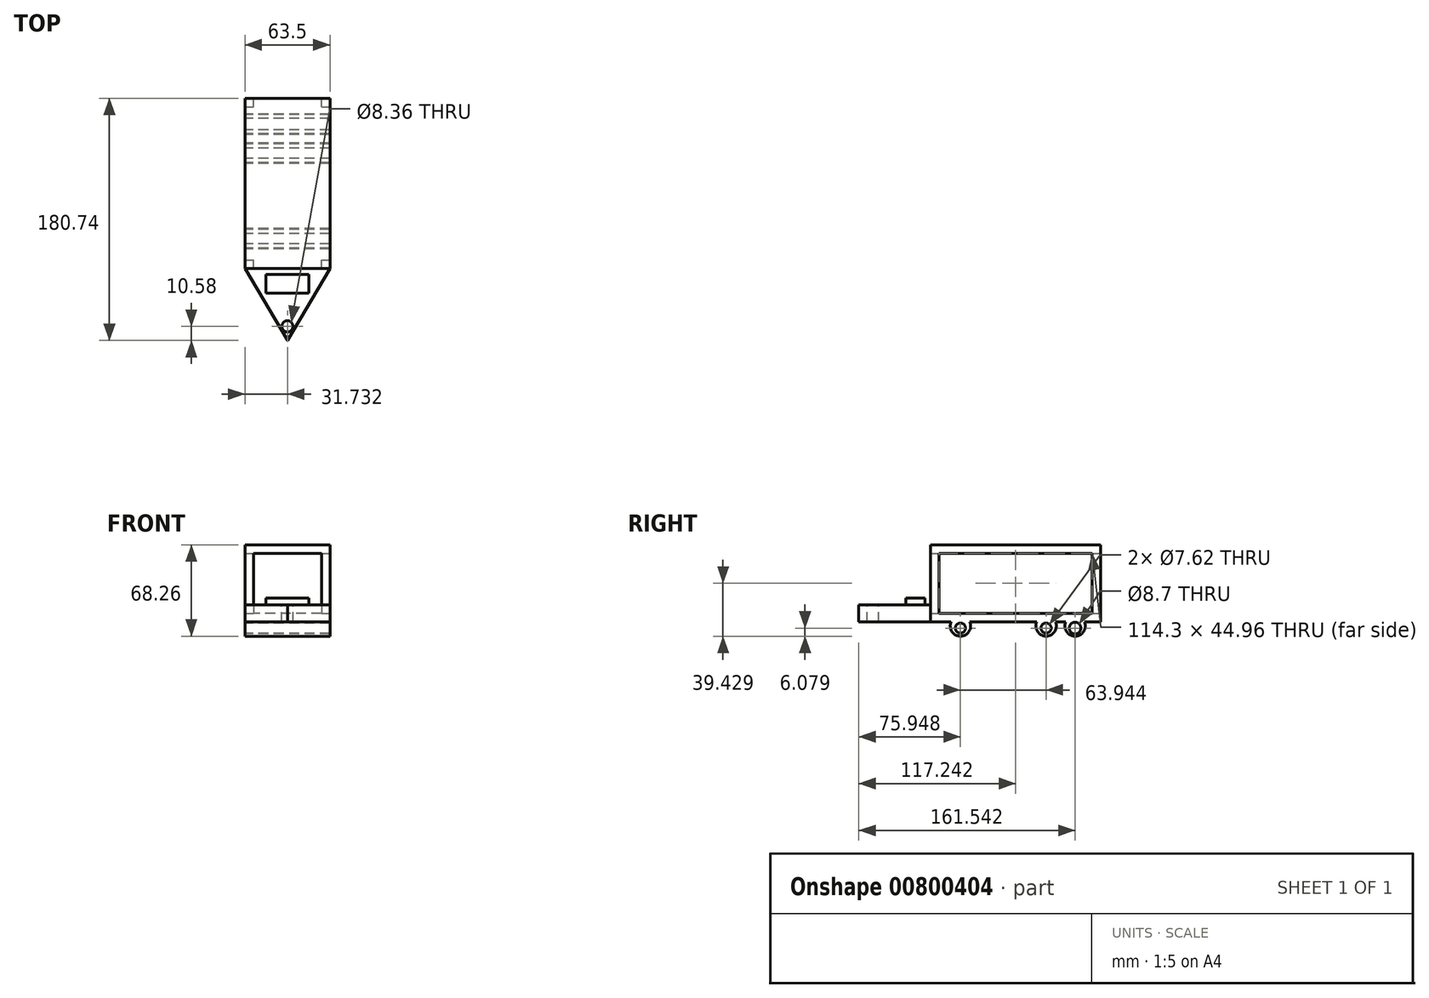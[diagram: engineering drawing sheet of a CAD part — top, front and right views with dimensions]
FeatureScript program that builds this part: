
annotation { "Feature Type Name" : "Feature", "Feature Type Description" : "" }
export const myFeature = defineFeature(function(context is Context, id is Id, definition is map)
    precondition{}
    {
        {
            var Q0;
            Q0=qCreatedBy(makeId("Top.planeOp"),FACE);
            var sketch = newSketch(context, id + "F0", { "sketchPlane" : qUnion([Q0])});
            skLineSegment(sketch, "E0", {"start": v(-27.56, 101.28) * mm, "end": v(-27.56, -25.72) * mm});
            skLineSegment(sketch, "E1", {"start": v(-27.56, -25.72) * mm, "end": v(35.94, -25.72) * mm});
            skLineSegment(sketch, "E2", {"start": v(35.94, -25.72) * mm, "end": v(35.94, 101.28) * mm});
            skLineSegment(sketch, "E3", {"start": v(35.94, 101.28) * mm, "end": v(-27.56, 101.28) * mm});
            skSolve(sketch);
        }
        {
            var Q0;
            Q0=makeQuery(id+"F0.imprint","IMPRINT",FACE,{"disambiguationData":[TD([[makeQuery(id+"F0.imprint","IMPRINT",EDGE,{"derivedFrom":sQuery(id+"F0.wireOp",EDGE,"E0")}),1.0]])]});
            extrude(context, id + "F1", {"entities" : qUnion([Q0]), "depth" : 57.66 * mm, "offsetDistance" : 25.4 * mm});
        }
        {
            var Q0;
            Q0=makeQuery(id+"F1.opExtrude","CAP_FACE",FACE,{"disambiguationData":[OSD([sQuery(id+"F0.wireOp",EDGE,"E0"),sQuery(id+"F0.wireOp",EDGE,"E1"),sQuery(id+"F0.wireOp",EDGE,"E2"),sQuery(id+"F0.wireOp",EDGE,"E3")])],"isStart":false});
            var sketch = newSketch(context, id + "F2", { "sketchPlane" : qUnion([Q0])});
            skLineSegment(sketch, "E4.0", {"start": v(-21.21, -19.37) * mm, "end": v(29.59, -19.37) * mm});
            skLineSegment(sketch, "E5.0", {"start": v(-21.21, 94.93) * mm, "end": v(-21.21, -19.37) * mm});
            skLineSegment(sketch, "E6.0", {"start": v(29.59, 94.93) * mm, "end": v(-21.21, 94.93) * mm});
            skLineSegment(sketch, "E7.0", {"start": v(29.59, -19.37) * mm, "end": v(29.59, 94.93) * mm});
            skSolve(sketch);
        }
        {
            var Q0;
            Q0=makeQuery(id+"F2.imprint","IMPRINT",FACE,{"disambiguationData":[TD([[makeQuery(id+"F2.imprint","IMPRINT",EDGE,{"derivedFrom":sQuery(id+"F2.wireOp",EDGE,"E4.0")}),1.0]])]});
            extrude(context, id + "F3", {"entities" : qUnion([Q0]), "operationType" : NewBodyOperationType.REMOVE, "oppositeDirection" : true, "depth" : 155.7 * mm, "offsetDistance" : 25.4 * mm});
        }
        {
            var Q0;
            Q0=makeQuery(id+"F1.opExtrude","SWEPT_FACE",FACE,{"disambiguationData":[OSD([sQuery(id+"F0.wireOp",EDGE,"E2")])]});
            var sketch = newSketch(context, id + "F4", { "sketchPlane" : qUnion([Q0])});
            skLineSegment(sketch, "E8.0", {"start": v(-19.37, 101.6) * mm, "end": v(-19.37, 0) * mm});
            skLineSegment(sketch, "E9.0", {"start": v(-25.72, 6.35) * mm, "end": v(101.28, 6.35) * mm});
            skLineSegment(sketch, "E10.0", {"start": v(94.93, 101.6) * mm, "end": v(94.93, 0) * mm});
            skLineSegment(sketch, "E11.0", {"start": v(-25.72, 51.3) * mm, "end": v(101.28, 51.3) * mm});
            skSolve(sketch);
        }
        {
            var Q0;
            {var subQ0=sQuery(id+"F4.wireOp",EDGE,"E11.0");var subQ1=sQuery(id+"F4.wireOp",EDGE,"E8.0");var subQ2=makeQuery(id+"F4.imprint","INTERSECT",VERTEX,{"derivedFrom":[subQ1,subQ0]});Q0=makeQuery(id+"F4.imprint","IMPRINT",FACE,{"disambiguationData":[TD([[makeQuery(id+"F4.imprint","IMPRINT",EDGE,{"disambiguationData":[TD([[subQ2,-1.0]])],"derivedFrom":subQ1}),1.0]])]});}
            extrude(context, id + "F5", {"entities" : qUnion([Q0]), "operationType" : NewBodyOperationType.REMOVE, "oppositeDirection" : true, "depth" : 96.77 * mm, "offsetDistance" : 25.4 * mm});
        }
        {
            var Q0;
            Q0=makeQuery(id+"F1.opExtrude","SWEPT_FACE",FACE,{"disambiguationData":[OSD([sQuery(id+"F0.wireOp",EDGE,"E3")])]});
            var sketch = newSketch(context, id + "F6", { "sketchPlane" : qUnion([Q0])});
            skLineSegment(sketch, "E12.0", {"start": v(-35.94, 51.3) * mm, "end": v(27.56, 51.3) * mm});
            skLineSegment(sketch, "E13.0", {"start": v(-29.59, 101.6) * mm, "end": v(-29.59, 0) * mm});
            skLineSegment(sketch, "E14.0", {"start": v(-35.94, 6.35) * mm, "end": v(27.56, 6.35) * mm});
            skLineSegment(sketch, "E15.0", {"start": v(21.21, 101.6) * mm, "end": v(21.21, 0) * mm});
            skSolve(sketch);
        }
        {
            var Q0;
            {var subQ0=sQuery(id+"F6.wireOp",EDGE,"E13.0");var subQ1=sQuery(id+"F6.wireOp",EDGE,"E12.0");var subQ2=makeQuery(id+"F6.imprint","INTERSECT",VERTEX,{"derivedFrom":[subQ1,subQ0]});Q0=makeQuery(id+"F6.imprint","IMPRINT",FACE,{"disambiguationData":[TD([[makeQuery(id+"F6.imprint","IMPRINT",EDGE,{"disambiguationData":[TD([[subQ2,-1.0]])],"derivedFrom":subQ1}),-1.0]])]});}
            extrude(context, id + "F7", {"entities" : qUnion([Q0]), "operationType" : NewBodyOperationType.REMOVE, "oppositeDirection" : true, "depth" : 127 * mm, "offsetDistance" : 25.4 * mm});
        }
        {
            var Q0;
            {var subQ2=makeQuery(id+"F3.boolean.opBoolean","COPY",FACE,{"derivedFrom":makeQuery(id+"F3.opExtrude","SWEPT_FACE",FACE,{"disambiguationData":[OSD([sQuery(id+"F2.wireOp",EDGE,"E4.0")])]})});var subQ4=makeQuery(id+"F5.opExtrude","SWEPT_FACE",FACE,{"disambiguationData":[OSD([sQuery(id+"F4.wireOp",EDGE,"E8.0")])]});var subQ5=sQuery(id+"F0.wireOp",EDGE,"E0");var subQ8=sQuery(id+"F0.wireOp",EDGE,"E2");Q0=makeQuery(id+"F7.boolean.opBoolean","SPLIT",FACE,{"disambiguationData":[TD([makeQuery(id+"F1.opExtrude","CAP_FACE",FACE,{"disambiguationData":[OSD([subQ5,sQuery(id+"F0.wireOp",EDGE,"E1"),subQ8,sQuery(id+"F0.wireOp",EDGE,"E3")])],"isStart":true})])],"derivedFrom":makeQuery(id+"F5.boolean.opBoolean","MERGE",FACE,{"derivedFrom":[subQ2,subQ4]})});}
            extrude(context, id + "F8", {"entities" : qUnion([Q0]), "operationType" : NewBodyOperationType.ADD, "depth" : 120.14 * mm, "offsetDistance" : 25.4 * mm});
        }
        {
            var Q0;
            {var subQ1=makeQuery(id+"F5.opExtrude","SWEPT_FACE",FACE,{"disambiguationData":[OSD([sQuery(id+"F4.wireOp",EDGE,"E8.0")])]});var subQ2=makeQuery(id+"F3.boolean.opBoolean","COPY",FACE,{"derivedFrom":makeQuery(id+"F3.opExtrude","SWEPT_FACE",FACE,{"disambiguationData":[OSD([sQuery(id+"F2.wireOp",EDGE,"E4.0")])]})});var subQ4=sQuery(id+"F0.wireOp",EDGE,"E2");var subQ5=sQuery(id+"F0.wireOp",EDGE,"E0");Q0=makeQuery(id+"F7.boolean.opBoolean","SPLIT",FACE,{"disambiguationData":[TD([makeQuery(id+"F1.opExtrude","CAP_FACE",FACE,{"disambiguationData":[OSD([subQ5,sQuery(id+"F0.wireOp",EDGE,"E1"),subQ4,sQuery(id+"F0.wireOp",EDGE,"E3")])],"isStart":false})])],"derivedFrom":makeQuery(id+"F5.boolean.opBoolean","MERGE",FACE,{"derivedFrom":[subQ2,subQ1]})});}
            extrude(context, id + "F9", {"entities" : qUnion([Q0]), "operationType" : NewBodyOperationType.ADD, "depth" : 115.82 * mm, "offsetDistance" : 25.4 * mm});
        }
        {
            var Q0;
            Q0=qCreatedBy(makeId("Top.planeOp"),FACE);
            var sketch = newSketch(context, id + "F10", { "sketchPlane" : qUnion([Q0])});
            skLineSegment(sketch, "E16.0", {"start": v(-27.56, -25.72) * mm, "end": v(35.94, -25.72) * mm});
            skLineSegment(sketch, "E17", {"start": v(4.19, -25.72) * mm, "end": v(4.19, -79.46) * mm});
            skLineSegment(sketch, "E18", {"start": v(4.19, -79.46) * mm, "end": v(-27.56, -25.72) * mm});
            skLineSegment(sketch, "E19", {"start": v(35.94, -25.72) * mm, "end": v(4.19, -79.46) * mm});
            skSolve(sketch);
        }
        {
            var Q0;
            Q0=qSketchRegion(id+"F10",true);
            extrude(context, id + "F11", {"entities" : qUnion([Q0]), "operationType" : NewBodyOperationType.ADD, "depth" : 12.7 * mm, "offsetDistance" : 25.4 * mm});
        }
        {
            var Q0;
            Q0=makeQuery(id+"F11.opExtrude","CAP_FACE",FACE,{"disambiguationData":[OSD([sQuery(id+"F10.wireOp",EDGE,"E16.0"),sQuery(id+"F10.wireOp",EDGE,"E18"),sQuery(id+"F10.wireOp",EDGE,"E19")])],"isStart":false});
            var sketch = newSketch(context, id + "F12", { "sketchPlane" : qUnion([Q0])});
            skCircle(sketch, "E20", {"center": v(4.17, -68.88) * mm, "radius": 4.18 * mm});
            skLineSegment(sketch, "E21.0", {"start": v(-21.21, -25.72) * mm, "end": v(29.59, -25.72) * mm});
            skLineSegment(sketch, "E22.0", {"start": v(35.94, -25.72) * mm, "end": v(4.19, -79.46) * mm});
            skLineSegment(sketch, "E23.0", {"start": v(4.19, -79.46) * mm, "end": v(-27.56, -25.72) * mm});
            skLineSegment(sketch, "E24", {"start": v(4.19, -25.72) * mm, "end": v(4.19, -79.46) * mm});
            skSolve(sketch);
        }
        {
            var Q0;
            {var subQ0=sQuery(id+"F12.wireOp",EDGE,"E24");var subQ1=sQuery(id+"F12.wireOp",EDGE,"E20");var subQ2=makeQuery(id+"F12.imprint","INTERSECT",VERTEX,{"disambiguationData":[OD(0.0)],"derivedFrom":[subQ1,subQ0]});Q0=makeQuery(id+"F12.imprint","IMPRINT",FACE,{"disambiguationData":[TD([[makeQuery(id+"F12.imprint","IMPRINT",EDGE,{"disambiguationData":[TD([[subQ2,-1.0]])],"derivedFrom":subQ1}),1.0]])]});}
            var Q1;
            {var subQ0=sQuery(id+"F12.wireOp",EDGE,"E24");var subQ1=sQuery(id+"F12.wireOp",EDGE,"E20");var subQ2=makeQuery(id+"F12.imprint","INTERSECT",VERTEX,{"disambiguationData":[OD(0.0)],"derivedFrom":[subQ1,subQ0]});Q1=makeQuery(id+"F12.imprint","IMPRINT",FACE,{"disambiguationData":[TD([[makeQuery(id+"F12.imprint","IMPRINT",EDGE,{"disambiguationData":[TD([[subQ2,1.0]])],"derivedFrom":subQ1}),1.0]])]});}
            extrude(context, id + "F13", {"entities" : qUnion([Q0, Q1]), "operationType" : NewBodyOperationType.REMOVE, "oppositeDirection" : true, "depth" : 25.4 * mm, "offsetDistance" : 25.4 * mm});
        }
        {
            var Q0;
            Q0=makeQuery(id+"F11.opExtrude","CAP_FACE",FACE,{"disambiguationData":[OSD([sQuery(id+"F10.wireOp",EDGE,"E16.0"),sQuery(id+"F10.wireOp",EDGE,"E18"),sQuery(id+"F10.wireOp",EDGE,"E19")])],"isStart":false});
            var sketch = newSketch(context, id + "F14", { "sketchPlane" : qUnion([Q0])});
            skLineSegment(sketch, "E25.bottom", {"start": v(-11.82, -29.99) * mm, "end": v(20.03, -29.99) * mm});
            skLineSegment(sketch, "E25.top", {"start": v(-11.82, -44.18) * mm, "end": v(20.03, -44.18) * mm});
            skLineSegment(sketch, "E25.left", {"start": v(-11.82, -29.99) * mm, "end": v(-11.82, -44.18) * mm});
            skLineSegment(sketch, "E25.right", {"start": v(20.03, -29.99) * mm, "end": v(20.03, -44.18) * mm});
            skSolve(sketch);
        }
        {
            var Q0;
            Q0=qSketchRegion(id+"F14",true);
            extrude(context, id + "F15", {"entities" : qUnion([Q0]), "operationType" : NewBodyOperationType.ADD, "depth" : 5.08 * mm, "offsetDistance" : 25.4 * mm});
        }
        {
            var Q0;
            Q0=makeQuery(id+"F1.opExtrude","SWEPT_FACE",FACE,{"disambiguationData":[OSD([sQuery(id+"F0.wireOp",EDGE,"E0")])]});
            var sketch = newSketch(context, id + "F16", { "sketchPlane" : qUnion([Q0])});
            skArc(sketch, "E26", {"start": v(-89.1, 0) * mm, "mid": v(-82.08, -10.6) * mm, "end": v(-75.07, 0) * mm});
            skArc(sketch, "E27", {"start": v(-67.45, 0) * mm, "mid": v(-60.43, -10.6) * mm, "end": v(-53.42, 0) * mm});
            skArc(sketch, "E28", {"start": v(-3.5, 0) * mm, "mid": v(3.51, -10.6) * mm, "end": v(10.53, 0) * mm});
            skCircle(sketch, "E29", {"center": v(-82.08, -4.52) * mm, "radius": 4.35 * mm});
            skCircle(sketch, "E30", {"center": v(-60.43, -4.52) * mm, "radius": 3.81 * mm});
            skCircle(sketch, "E31", {"center": v(3.51, -4.52) * mm, "radius": 3.81 * mm});
            skSolve(sketch);
        }
        {
            var Q0;
            Q0=qSketchRegion(id+"F16",true);
            var Q1;
            {var subQ0=sQuery(id+"F16.wireOp",EDGE,"E26");Q1=makeQuery(id+"F16.imprint","IMPRINT",FACE,{"disambiguationData":[TD([[makeQuery(id+"F16.imprint","IMPRINT",EDGE,{"derivedFrom":subQ0}),1.0]])]});}
            var Q2;
            {var subQ0=sQuery(id+"F16.wireOp",EDGE,"E27");Q2=makeQuery(id+"F16.imprint","IMPRINT",FACE,{"disambiguationData":[TD([[makeQuery(id+"F16.imprint","IMPRINT",EDGE,{"derivedFrom":subQ0}),1.0]])]});}
            var Q3;
            {var subQ0=sQuery(id+"F16.wireOp",EDGE,"E28");Q3=makeQuery(id+"F16.imprint","IMPRINT",FACE,{"disambiguationData":[TD([[makeQuery(id+"F16.imprint","IMPRINT",EDGE,{"derivedFrom":subQ0}),1.0]])]});}
            extrude(context, id + "F17", {"entities" : qUnion([Q0, Q1, Q2, Q3]), "operationType" : NewBodyOperationType.ADD, "oppositeDirection" : true, "depth" : 63.5 * mm, "offsetDistance" : 25.4 * mm});
        }
        {
            var Q0;
            Q0=qSketchRegion(id+"F16",true);
            extrude(context, id + "F18", {"entities" : qUnion([Q0]), "operationType" : NewBodyOperationType.REMOVE, "oppositeDirection" : true, "depth" : 94.49 * mm, "offsetDistance" : 25.4 * mm});
        }
    });
